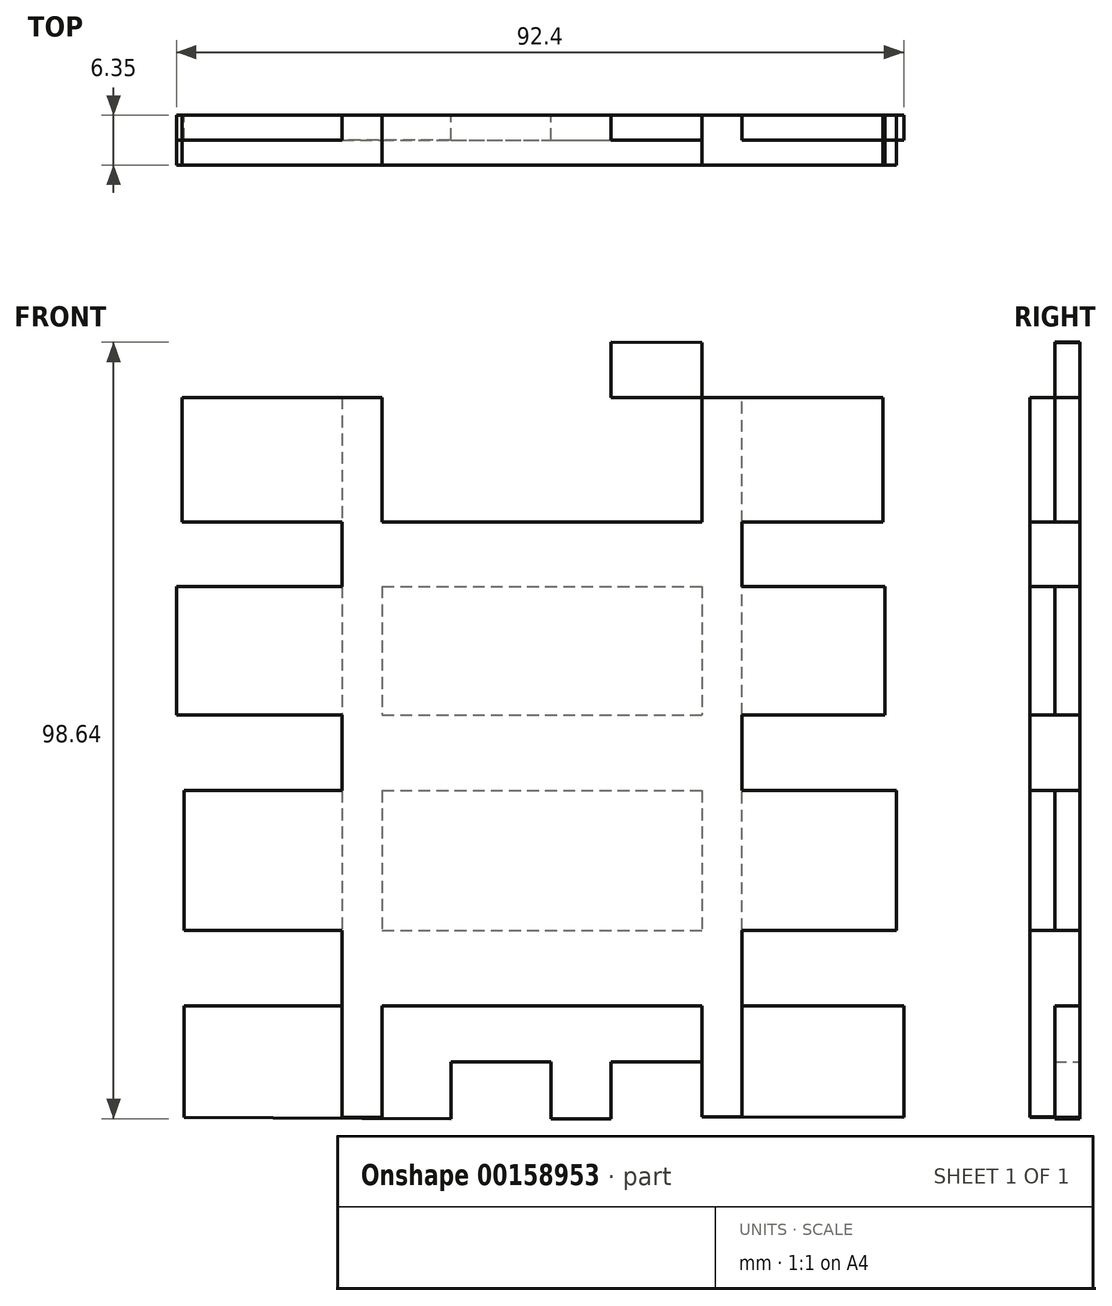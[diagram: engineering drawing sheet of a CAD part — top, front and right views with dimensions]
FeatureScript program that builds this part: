
annotation { "Feature Type Name" : "Feature", "Feature Type Description" : "" }
export const myFeature = defineFeature(function(context is Context, id is Id, definition is map)
    precondition{}
    {
        {
            var Q0;
            Q0=qCreatedBy(makeId("Front.planeOp"),FACE);
            var sketch = newSketch(context, id + "F0", { "sketchPlane" : qUnion([Q0])});
            skLineSegment(sketch, "E0.left", {"start": v(-28.43, 40.31) * mm, "end": v(-28.43, -51.12) * mm});
            skLineSegment(sketch, "E1.bottom", {"start": v(-48.77, 40.31) * mm, "end": v(40.26, 40.31) * mm});
            skLineSegment(sketch, "E1.top", {"start": v(-48.77, 24.47) * mm, "end": v(40.26, 24.47) * mm});
            skLineSegment(sketch, "E1.left", {"start": v(-48.77, 40.31) * mm, "end": v(-48.77, 24.47) * mm});
            skLineSegment(sketch, "E1.right", {"start": v(40.26, 40.31) * mm, "end": v(40.26, 24.47) * mm});
            skLineSegment(sketch, "E2.bottom", {"start": v(-49.49, 16.31) * mm, "end": v(40.5, 16.31) * mm});
            skLineSegment(sketch, "E2.top", {"start": v(-49.49, 0) * mm, "end": v(40.5, 0) * mm});
            skLineSegment(sketch, "E2.left", {"start": v(-49.49, 16.31) * mm, "end": v(-49.49, 0) * mm});
            skLineSegment(sketch, "E2.right", {"start": v(40.5, 16.31) * mm, "end": v(40.5, 0) * mm});
            skLineSegment(sketch, "E3.bottom", {"start": v(-48.51, -9.6) * mm, "end": v(41.95, -9.6) * mm});
            skLineSegment(sketch, "E3.top", {"start": v(-48.51, -27.36) * mm, "end": v(41.95, -27.36) * mm});
            skLineSegment(sketch, "E3.left", {"start": v(-48.51, -9.6) * mm, "end": v(-48.51, -27.36) * mm});
            skLineSegment(sketch, "E3.right", {"start": v(41.95, -9.6) * mm, "end": v(41.95, -27.36) * mm});
            skLineSegment(sketch, "E4.bottom", {"start": v(-48.51, -36.96) * mm, "end": v(42.91, -36.96) * mm});
            skLineSegment(sketch, "E4.left", {"start": v(-48.51, -36.96) * mm, "end": v(-48.51, -51.12) * mm});
            skLineSegment(sketch, "E4.right", {"start": v(42.91, -36.96) * mm, "end": v(42.91, -51.12) * mm});
            skLineSegment(sketch, "E5.top", {"start": v(-28.43, -51.12) * mm, "end": v(-23.35, -51.12) * mm});
            skLineSegment(sketch, "E5.right", {"start": v(-23.35, 40.31) * mm, "end": v(-23.35, -51.12) * mm});
            skLineSegment(sketch, "E6.top", {"start": v(22.37, -51.1) * mm, "end": v(17.3, -51.1) * mm});
            skLineSegment(sketch, "E6.right", {"start": v(17.3, 47.27) * mm, "end": v(17.3, -51.1) * mm});
            skLineSegment(sketch, "E7", {"start": v(-28.43, 40.31) * mm, "end": v(5.7, 40.31) * mm});
            skLineSegment(sketch, "E8", {"start": v(5.7, 40.31) * mm, "end": v(5.7, 47.34) * mm});
            skLineSegment(sketch, "E9", {"start": v(17.3, 47.27) * mm, "end": v(17.3, 40.31) * mm});
            skLineSegment(sketch, "E10.bottom", {"start": v(-14.61, 40.31) * mm, "end": v(-1.91, 40.31) * mm});
            skLineSegment(sketch, "E10.top", {"start": v(-14.61, 47.51) * mm, "end": v(-1.91, 47.51) * mm});
            skLineSegment(sketch, "E10.left", {"start": v(-14.61, 40.31) * mm, "end": v(-14.61, 47.51) * mm});
            skLineSegment(sketch, "E10.right", {"start": v(-1.91, 40.31) * mm, "end": v(-1.91, 47.51) * mm});
            skLineSegment(sketch, "E11", {"start": v(-14.61, -51.3) * mm, "end": v(-48.51, -51.12) * mm});
            skLineSegment(sketch, "E12.top", {"start": v(-14.61, -44.1) * mm, "end": v(-1.91, -44.1) * mm});
            skLineSegment(sketch, "E12.left", {"start": v(-14.61, -51.3) * mm, "end": v(-14.61, -44.1) * mm});
            skLineSegment(sketch, "E12.right", {"start": v(-1.91, -51.3) * mm, "end": v(-1.91, -44.1) * mm});
            skLineSegment(sketch, "E13", {"start": v(-1.91, -51.3) * mm, "end": v(5.7, -51.3) * mm});
            skLineSegment(sketch, "E14.top", {"start": v(5.7, -44.1) * mm, "end": v(17.3, -44.1) * mm});
            skLineSegment(sketch, "E14.left", {"start": v(5.7, -51.3) * mm, "end": v(5.7, -44.1) * mm});
            skLineSegment(sketch, "E14.right", {"start": v(17.3, -51.3) * mm, "end": v(17.3, -44.1) * mm});
            skLineSegment(sketch, "E15", {"start": v(22.37, -51.1) * mm, "end": v(42.91, -51.12) * mm});
            skLineSegment(sketch, "E16", {"start": v(5.7, 47.34) * mm, "end": v(17.3, 47.27) * mm});
            skLineSegment(sketch, "E17", {"start": v(22.37, -51.1) * mm, "end": v(22.37, 40.31) * mm});
            skSolve(sketch);
        }
        {
            var Q0;
            {var subQ10=sQuery(id+"F0.wireOp",EDGE,"E10.bottom");Q0=makeQuery(id+"F0.imprint","IMPRINT",FACE,{"disambiguationData":[TD([[makeQuery(id+"F0.imprint","IMPRINT",EDGE,{"derivedFrom":subQ10}),-1.0]])]});}
            var Q1;
            {var subQ0=sQuery(id+"F0.wireOp",EDGE,"E5.right");var subQ1=sQuery(id+"F0.wireOp",EDGE,"E2.bottom");var subQ2=makeQuery(id+"F0.imprint","INTERSECT",VERTEX,{"derivedFrom":[subQ1,subQ0]});Q1=makeQuery(id+"F0.imprint","IMPRINT",FACE,{"disambiguationData":[TD([[makeQuery(id+"F0.imprint","IMPRINT",EDGE,{"disambiguationData":[TD([[subQ2,-1.0]])],"derivedFrom":subQ1}),-1.0]])]});}
            var Q2;
            {var subQ0=sQuery(id+"F0.wireOp",EDGE,"E5.right");var subQ1=sQuery(id+"F0.wireOp",EDGE,"E3.bottom");var subQ2=makeQuery(id+"F0.imprint","INTERSECT",VERTEX,{"derivedFrom":[subQ1,subQ0]});Q2=makeQuery(id+"F0.imprint","IMPRINT",FACE,{"disambiguationData":[TD([[makeQuery(id+"F0.imprint","IMPRINT",EDGE,{"disambiguationData":[TD([[subQ2,-1.0]])],"derivedFrom":subQ1}),-1.0]])]});}
            var Q3;
            {var subQ0=sQuery(id+"F0.wireOp",EDGE,"E5.right");var subQ1=sQuery(id+"F0.wireOp",EDGE,"E4.bottom");var subQ2=makeQuery(id+"F0.imprint","INTERSECT",VERTEX,{"derivedFrom":[subQ1,subQ0]});Q3=makeQuery(id+"F0.imprint","IMPRINT",FACE,{"disambiguationData":[TD([[makeQuery(id+"F0.imprint","IMPRINT",EDGE,{"disambiguationData":[TD([[subQ2,-1.0]])],"derivedFrom":subQ1}),-1.0]])]});}
            var Q4;
            {var subQ0=sQuery(id+"F0.wireOp",EDGE,"E4.left");Q4=makeQuery(id+"F0.imprint","IMPRINT",FACE,{"disambiguationData":[TD([[makeQuery(id+"F0.imprint","IMPRINT",EDGE,{"derivedFrom":subQ0}),1.0]])]});}
            var Q5;
            {var subQ0=sQuery(id+"F0.wireOp",EDGE,"E3.left");Q5=makeQuery(id+"F0.imprint","IMPRINT",FACE,{"disambiguationData":[TD([[makeQuery(id+"F0.imprint","IMPRINT",EDGE,{"derivedFrom":subQ0}),1.0]])]});}
            var Q6;
            {var subQ0=sQuery(id+"F0.wireOp",EDGE,"E2.left");Q6=makeQuery(id+"F0.imprint","IMPRINT",FACE,{"disambiguationData":[TD([[makeQuery(id+"F0.imprint","IMPRINT",EDGE,{"derivedFrom":subQ0}),1.0]])]});}
            var Q7;
            {var subQ0=sQuery(id+"F0.wireOp",EDGE,"E1.left");Q7=makeQuery(id+"F0.imprint","IMPRINT",FACE,{"disambiguationData":[TD([[makeQuery(id+"F0.imprint","IMPRINT",EDGE,{"derivedFrom":subQ0}),1.0]])]});}
            var Q8;
            {var subQ0=sQuery(id+"F0.wireOp",EDGE,"E1.right");Q8=makeQuery(id+"F0.imprint","IMPRINT",FACE,{"disambiguationData":[TD([[makeQuery(id+"F0.imprint","IMPRINT",EDGE,{"derivedFrom":subQ0}),-1.0]])]});}
            var Q9;
            {var subQ0=sQuery(id+"F0.wireOp",EDGE,"E2.right");Q9=makeQuery(id+"F0.imprint","IMPRINT",FACE,{"disambiguationData":[TD([[makeQuery(id+"F0.imprint","IMPRINT",EDGE,{"derivedFrom":subQ0}),-1.0]])]});}
            var Q10;
            {var subQ0=sQuery(id+"F0.wireOp",EDGE,"E3.right");Q10=makeQuery(id+"F0.imprint","IMPRINT",FACE,{"disambiguationData":[TD([[makeQuery(id+"F0.imprint","IMPRINT",EDGE,{"derivedFrom":subQ0}),-1.0]])]});}
            var Q11;
            {var subQ0=sQuery(id+"F0.wireOp",EDGE,"E4.right");Q11=makeQuery(id+"F0.imprint","IMPRINT",FACE,{"disambiguationData":[TD([[makeQuery(id+"F0.imprint","IMPRINT",EDGE,{"derivedFrom":subQ0}),-1.0]])]});}
            var Q12;
            Q12=makeQuery(id+"F0.imprint","IMPRINT",FACE,{"disambiguationData":[TD([[makeQuery(id+"F0.imprint","IMPRINT",EDGE,{"derivedFrom":sQuery(id+"F0.wireOp",EDGE,"E10.bottom")}),1.0]])]});
            var Q13;
            Q13=makeQuery(id+"F0.imprint","IMPRINT",FACE,{"disambiguationData":[TD([[makeQuery(id+"F0.imprint","IMPRINT",EDGE,{"derivedFrom":sQuery(id+"F0.wireOp",EDGE,"E6.bottom")}),-1.0]])]});
            var Q14;
            {var subQ2=sQuery(id+"F0.wireOp",EDGE,"E8");Q14=makeQuery(id+"F0.imprint","IMPRINT",FACE,{"disambiguationData":[TD([[makeQuery(id+"F0.imprint","IMPRINT",EDGE,{"derivedFrom":subQ2}),-1.0]])]});}
            extrude(context, id + "F1", {"entities" : qUnion([Q0, Q1, Q2, Q3, Q4, Q5, Q6, Q7, Q8, Q9, Q10, Q11, Q12, Q13, Q14]), "depth" : 3.17 * mm});
        }
        {
            var Q0;
            {var subQ0=sQuery(id+"F0.wireOp",EDGE,"E0.left");var subQ1=sQuery(id+"F0.wireOp",EDGE,"E1.top");var subQ2=makeQuery(id+"F0.imprint","INTERSECT",VERTEX,{"derivedFrom":[subQ1,subQ0]});Q0=makeQuery(id+"F0.imprint","IMPRINT",FACE,{"disambiguationData":[TD([[makeQuery(id+"F0.imprint","IMPRINT",EDGE,{"disambiguationData":[TD([[subQ2,-1.0]])],"derivedFrom":subQ1}),-1.0]])]});}
            var Q1;
            {var subQ0=sQuery(id+"F0.wireOp",EDGE,"E0.left");var subQ1=sQuery(id+"F0.wireOp",EDGE,"E1.top");var subQ2=makeQuery(id+"F0.imprint","INTERSECT",VERTEX,{"derivedFrom":[subQ1,subQ0]});Q1=makeQuery(id+"F0.imprint","IMPRINT",FACE,{"disambiguationData":[TD([[makeQuery(id+"F0.imprint","IMPRINT",EDGE,{"disambiguationData":[TD([[subQ2,-1.0]])],"derivedFrom":subQ1}),1.0]])]});}
            var Q2;
            {var subQ0=sQuery(id+"F0.wireOp",EDGE,"E0.left");var subQ1=sQuery(id+"F0.wireOp",EDGE,"E2.bottom");var subQ2=makeQuery(id+"F0.imprint","INTERSECT",VERTEX,{"derivedFrom":[subQ1,subQ0]});Q2=makeQuery(id+"F0.imprint","IMPRINT",FACE,{"disambiguationData":[TD([[makeQuery(id+"F0.imprint","IMPRINT",EDGE,{"disambiguationData":[TD([[subQ2,-1.0]])],"derivedFrom":subQ1}),-1.0]])]});}
            var Q3;
            {var subQ0=sQuery(id+"F0.wireOp",EDGE,"E0.left");var subQ1=sQuery(id+"F0.wireOp",EDGE,"E2.top");var subQ2=makeQuery(id+"F0.imprint","INTERSECT",VERTEX,{"derivedFrom":[subQ1,subQ0]});Q3=makeQuery(id+"F0.imprint","IMPRINT",FACE,{"disambiguationData":[TD([[makeQuery(id+"F0.imprint","IMPRINT",EDGE,{"disambiguationData":[TD([[subQ2,-1.0]])],"derivedFrom":subQ1}),-1.0]])]});}
            var Q4;
            {var subQ0=sQuery(id+"F0.wireOp",EDGE,"E0.left");var subQ1=sQuery(id+"F0.wireOp",EDGE,"E3.bottom");var subQ2=makeQuery(id+"F0.imprint","INTERSECT",VERTEX,{"derivedFrom":[subQ1,subQ0]});Q4=makeQuery(id+"F0.imprint","IMPRINT",FACE,{"disambiguationData":[TD([[makeQuery(id+"F0.imprint","IMPRINT",EDGE,{"disambiguationData":[TD([[subQ2,-1.0]])],"derivedFrom":subQ1}),-1.0]])]});}
            var Q5;
            {var subQ0=sQuery(id+"F0.wireOp",EDGE,"E0.left");var subQ1=sQuery(id+"F0.wireOp",EDGE,"E3.top");var subQ2=makeQuery(id+"F0.imprint","INTERSECT",VERTEX,{"derivedFrom":[subQ1,subQ0]});Q5=makeQuery(id+"F0.imprint","IMPRINT",FACE,{"disambiguationData":[TD([[makeQuery(id+"F0.imprint","IMPRINT",EDGE,{"disambiguationData":[TD([[subQ2,-1.0]])],"derivedFrom":subQ1}),-1.0]])]});}
            var Q6;
            {var subQ5=sQuery(id+"F0.wireOp",EDGE,"E5.top");Q6=makeQuery(id+"F0.imprint","IMPRINT",FACE,{"disambiguationData":[TD([[makeQuery(id+"F0.imprint","IMPRINT",EDGE,{"derivedFrom":subQ5}),1.0]])]});}
            var Q7;
            {var subQ5=sQuery(id+"F0.wireOp",EDGE,"E6.top");Q7=makeQuery(id+"F0.imprint","IMPRINT",FACE,{"disambiguationData":[TD([[makeQuery(id+"F0.imprint","IMPRINT",EDGE,{"derivedFrom":subQ5}),-1.0]])]});}
            var Q8;
            {var subQ0=sQuery(id+"F0.wireOp",EDGE,"E17");var subQ1=sQuery(id+"F0.wireOp",EDGE,"E3.top");var subQ2=makeQuery(id+"F0.imprint","INTERSECT",VERTEX,{"derivedFrom":[subQ1,subQ0]});Q8=makeQuery(id+"F0.imprint","IMPRINT",FACE,{"disambiguationData":[TD([[makeQuery(id+"F0.imprint","IMPRINT",EDGE,{"disambiguationData":[TD([[subQ2,1.0]])],"derivedFrom":subQ1}),-1.0]])]});}
            var Q9;
            {var subQ0=sQuery(id+"F0.wireOp",EDGE,"E17");var subQ1=sQuery(id+"F0.wireOp",EDGE,"E3.bottom");var subQ2=makeQuery(id+"F0.imprint","INTERSECT",VERTEX,{"derivedFrom":[subQ1,subQ0]});Q9=makeQuery(id+"F0.imprint","IMPRINT",FACE,{"disambiguationData":[TD([[makeQuery(id+"F0.imprint","IMPRINT",EDGE,{"disambiguationData":[TD([[subQ2,1.0]])],"derivedFrom":subQ1}),-1.0]])]});}
            var Q10;
            {var subQ0=sQuery(id+"F0.wireOp",EDGE,"E17");var subQ1=sQuery(id+"F0.wireOp",EDGE,"E2.top");var subQ2=makeQuery(id+"F0.imprint","INTERSECT",VERTEX,{"derivedFrom":[subQ1,subQ0]});Q10=makeQuery(id+"F0.imprint","IMPRINT",FACE,{"disambiguationData":[TD([[makeQuery(id+"F0.imprint","IMPRINT",EDGE,{"disambiguationData":[TD([[subQ2,1.0]])],"derivedFrom":subQ1}),-1.0]])]});}
            var Q11;
            {var subQ0=sQuery(id+"F0.wireOp",EDGE,"E17");var subQ1=sQuery(id+"F0.wireOp",EDGE,"E2.bottom");var subQ2=makeQuery(id+"F0.imprint","INTERSECT",VERTEX,{"derivedFrom":[subQ1,subQ0]});Q11=makeQuery(id+"F0.imprint","IMPRINT",FACE,{"disambiguationData":[TD([[makeQuery(id+"F0.imprint","IMPRINT",EDGE,{"disambiguationData":[TD([[subQ2,1.0]])],"derivedFrom":subQ1}),-1.0]])]});}
            var Q12;
            {var subQ0=sQuery(id+"F0.wireOp",EDGE,"E17");var subQ1=sQuery(id+"F0.wireOp",EDGE,"E1.top");var subQ2=makeQuery(id+"F0.imprint","INTERSECT",VERTEX,{"derivedFrom":[subQ1,subQ0]});Q12=makeQuery(id+"F0.imprint","IMPRINT",FACE,{"disambiguationData":[TD([[makeQuery(id+"F0.imprint","IMPRINT",EDGE,{"disambiguationData":[TD([[subQ2,1.0]])],"derivedFrom":subQ1}),-1.0]])]});}
            var Q13;
            {var subQ3=sQuery(id+"F0.wireOp",EDGE,"E17");var subQ5=sQuery(id+"F0.wireOp",EDGE,"E1.top");var subQ6=makeQuery(id+"F0.imprint","INTERSECT",VERTEX,{"derivedFrom":[subQ5,subQ3]});Q13=makeQuery(id+"F0.imprint","IMPRINT",FACE,{"disambiguationData":[TD([[makeQuery(id+"F0.imprint","IMPRINT",EDGE,{"disambiguationData":[TD([[subQ6,1.0]])],"derivedFrom":subQ5}),1.0]])]});}
            extrude(context, id + "F2", {"entities" : qUnion([Q0, Q1, Q2, Q3, Q4, Q5, Q6, Q7, Q8, Q9, Q10, Q11, Q12, Q13]), "depth" : 6.35 * mm});
        }
    });
